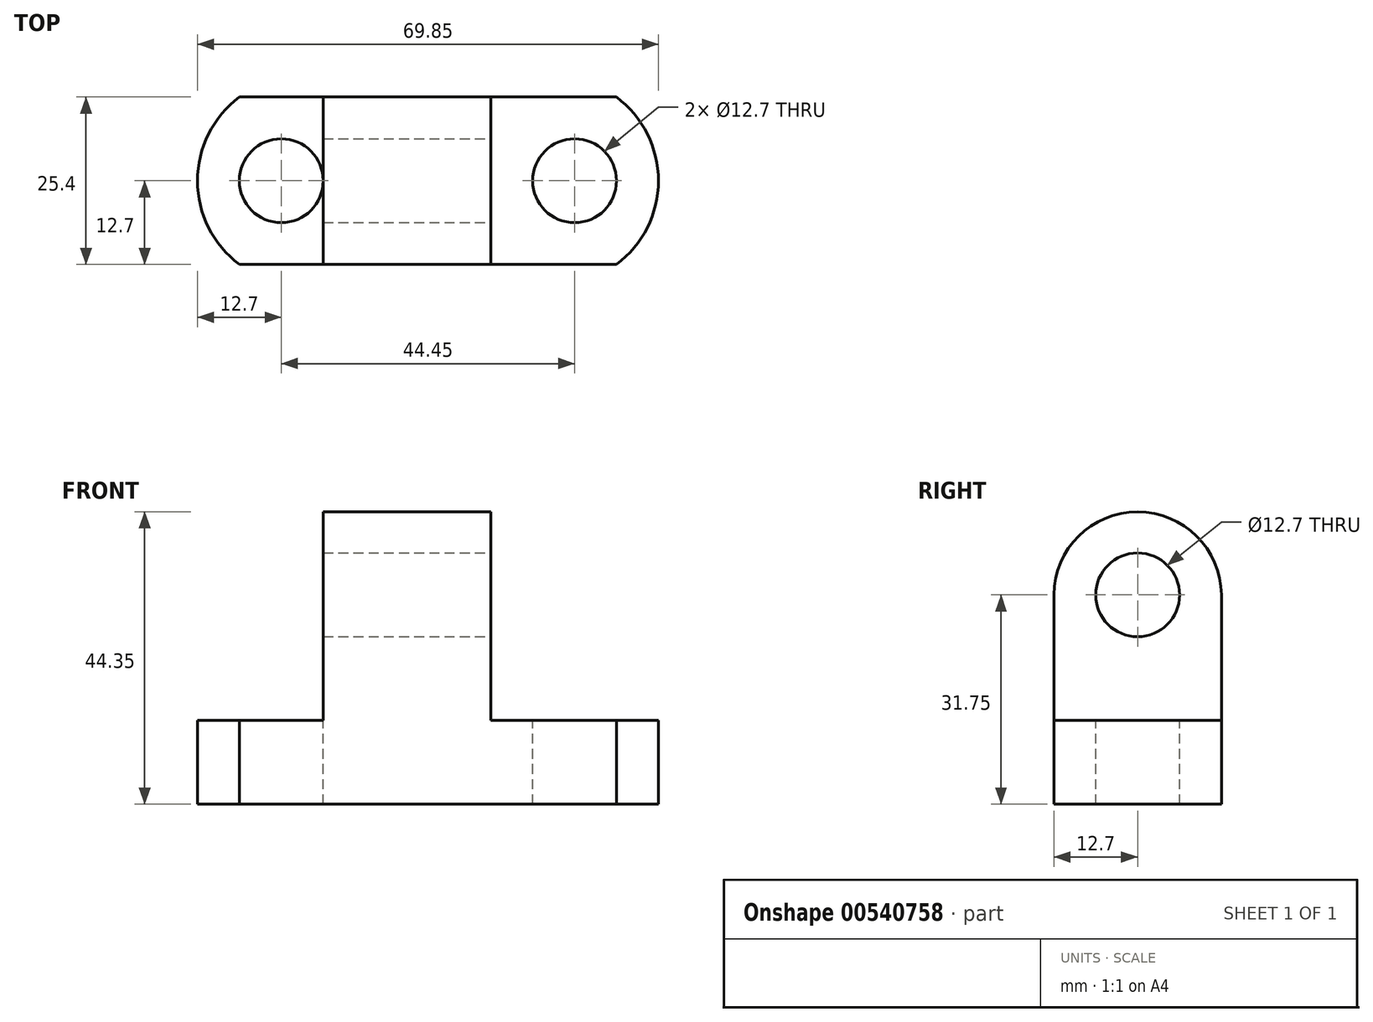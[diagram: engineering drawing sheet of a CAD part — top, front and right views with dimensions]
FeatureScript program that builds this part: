
annotation { "Feature Type Name" : "Feature", "Feature Type Description" : "" }
export const myFeature = defineFeature(function(context is Context, id is Id, definition is map)
    precondition{}
    {
        {
            var Q0;
            Q0=qCreatedBy(makeId("Front.planeOp"),FACE);
            var sketch = newSketch(context, id + "F0", { "sketchPlane" : qUnion([Q0])});
            skLineSegment(sketch, "E0", {"start": v(0, 0) * mm, "end": v(69.85, 0) * mm});
            skLineSegment(sketch, "E1", {"start": v(69.85, 0) * mm, "end": v(69.85, 12.7) * mm});
            skLineSegment(sketch, "E2", {"start": v(69.85, 12.7) * mm, "end": v(44.45, 12.7) * mm});
            skLineSegment(sketch, "E3", {"start": v(44.45, 12.7) * mm, "end": v(44.45, 44.45) * mm});
            skLineSegment(sketch, "E4", {"start": v(44.45, 44.45) * mm, "end": v(19.05, 44.45) * mm});
            skLineSegment(sketch, "E5", {"start": v(19.05, 44.45) * mm, "end": v(19.05, 12.7) * mm});
            skLineSegment(sketch, "E6", {"start": v(19.05, 12.7) * mm, "end": v(0, 12.7) * mm});
            skLineSegment(sketch, "E7", {"start": v(0, 12.7) * mm, "end": v(0, 0) * mm});
            skSolve(sketch);
        }
        {
            var Q0;
            Q0 = qSketchRegion(id + "F0", true);
            extrude(context, id + "F1", {"entities" : qUnion([Q0]), "depth" : 25.4 * mm, "offsetDistance" : 25.4 * mm});
        }
        {
            var Q0;
            Q0=makeQuery(id+"F1.opExtrude","SWEPT_FACE",FACE,{"disambiguationData":[OSD([sQuery(id+"F0.wireOp",EDGE,"E2")])]});
            var sketch = newSketch(context, id + "F2", { "sketchPlane" : qUnion([Q0])});
            skCircle(sketch, "E8", {"center": v(57.15, -12.7) * mm, "radius": 6.35 * mm});
            skPoint(sketch, "E8.centerSnap0", {"position": v(57.15, 0) * mm});
            skArc(sketch, "E9", {"start": v(63.5, -25.4) * mm, "mid": v(69.85, -12.7) * mm, "end": v(63.5, 0) * mm});
            skCircle(sketch, "E10", {"center": v(12.7, -12.7) * mm, "radius": 6.35 * mm});
            skSolve(sketch);
        }
        {
            var Q0;
            Q0=makeQuery(id+"F2.imprint","IMPRINT",FACE,{"disambiguationData":[TD([[makeQuery(id+"F2.imprint","IMPRINT",EDGE,{"derivedFrom":sQuery(id+"F2.wireOp",EDGE,"E10")}),1.0]])]});
            var Q1;
            Q1=makeQuery(id+"F2.imprint","IMPRINT",FACE,{"disambiguationData":[TD([[makeQuery(id+"F2.imprint","IMPRINT",EDGE,{"derivedFrom":sQuery(id+"F2.wireOp",EDGE,"E8")}),1.0]])]});
            var Q2;
            {var subQ0=sQuery(id+"F2.wireOp",EDGE,"E9");var subQ1=sQuery(id+"F0.wireOp",EDGE,"E2");var subQ2=makeQuery(id+"F1.opExtrude","CAP_EDGE",EDGE,{"disambiguationData":[OSD([subQ1])],"isStart":false});var subQ3=makeQuery(id+"F2.imprint","INTERSECT",VERTEX,{"derivedFrom":[subQ2,subQ0]});Q2=makeQuery(id+"F2.imprint","IMPRINT",FACE,{"disambiguationData":[TD([[makeQuery(id+"F2.imprint","IMPRINT",EDGE,{"disambiguationData":[TD([[subQ3,-1.0]])],"derivedFrom":subQ0}),-1.0]])]});}
            var Q3;
            {var subQ0=sQuery(id+"F2.wireOp",EDGE,"E9");var subQ1=sQuery(id+"F0.wireOp",EDGE,"E2");var subQ2=makeQuery(id+"F1.opExtrude","CAP_EDGE",EDGE,{"disambiguationData":[OSD([subQ1])],"isStart":true});var subQ3=makeQuery(id+"F2.imprint","INTERSECT",VERTEX,{"derivedFrom":[subQ2,subQ0]});Q3=makeQuery(id+"F2.imprint","IMPRINT",FACE,{"disambiguationData":[TD([[makeQuery(id+"F2.imprint","IMPRINT",EDGE,{"disambiguationData":[TD([[subQ3,1.0]])],"derivedFrom":subQ0}),-1.0]])]});}
            extrude(context, id + "F3", {"entities" : qUnion([Q0, Q1, Q2, Q3]), "operationType" : NewBodyOperationType.REMOVE, "oppositeDirection" : true, "depth" : 25.4 * mm, "offsetDistance" : 25.4 * mm});
        }
        {
            var Q0;
            Q0=makeQuery(id+"F1.opExtrude","SWEPT_FACE",FACE,{"disambiguationData":[OSD([sQuery(id+"F0.wireOp",EDGE,"E6")])]});
            var sketch = newSketch(context, id + "F4", { "sketchPlane" : qUnion([Q0])});
            skArc(sketch, "E11", {"start": v(6.35, 0) * mm, "mid": v(0, -12.7) * mm, "end": v(6.35, -25.4) * mm});
            skSolve(sketch);
        }
        {
            var Q0;
            {var subQ0=sQuery(id+"F4.wireOp",EDGE,"E11");var subQ1=sQuery(id+"F0.wireOp",EDGE,"E6");var subQ2=makeQuery(id+"F1.opExtrude","CAP_EDGE",EDGE,{"disambiguationData":[OSD([subQ1])],"isStart":true});var subQ3=makeQuery(id+"F4.imprint","INTERSECT",VERTEX,{"derivedFrom":[subQ2,subQ0]});Q0=makeQuery(id+"F4.imprint","IMPRINT",FACE,{"disambiguationData":[TD([[makeQuery(id+"F4.imprint","IMPRINT",EDGE,{"disambiguationData":[TD([[subQ3,-1.0]])],"derivedFrom":subQ0}),-1.0]])]});}
            var Q1;
            {var subQ0=sQuery(id+"F4.wireOp",EDGE,"E11");var subQ1=sQuery(id+"F0.wireOp",EDGE,"E6");var subQ2=makeQuery(id+"F1.opExtrude","CAP_EDGE",EDGE,{"disambiguationData":[OSD([subQ1])],"isStart":false});var subQ3=makeQuery(id+"F4.imprint","INTERSECT",VERTEX,{"derivedFrom":[subQ2,subQ0]});Q1=makeQuery(id+"F4.imprint","IMPRINT",FACE,{"disambiguationData":[TD([[makeQuery(id+"F4.imprint","IMPRINT",EDGE,{"disambiguationData":[TD([[subQ3,1.0]])],"derivedFrom":subQ0}),-1.0]])]});}
            extrude(context, id + "F5", {"entities" : qUnion([Q0, Q1]), "operationType" : NewBodyOperationType.REMOVE, "oppositeDirection" : true, "depth" : 25.4 * mm, "offsetDistance" : 25.4 * mm});
        }
        {
            var Q0;
            Q0=makeQuery(id+"F1.opExtrude","SWEPT_FACE",FACE,{"disambiguationData":[OSD([sQuery(id+"F0.wireOp",EDGE,"E3")])]});
            var sketch = newSketch(context, id + "F6", { "sketchPlane" : qUnion([Q0])});
            skCircle(sketch, "E12", {"center": v(-12.7, 31.75) * mm, "radius": 6.35 * mm});
            skArc(sketch, "E13", {"start": v(0, 31.75) * mm, "mid": v(-12.7, 44.35) * mm, "end": v(-25.4, 31.75) * mm});
            skSolve(sketch);
        }
        {
            var Q0;
            {var subQ0=sQuery(id+"F6.wireOp",EDGE,"E13");Q0=makeQuery(id+"F6.imprint","IMPRINT",FACE,{"disambiguationData":[TD([[makeQuery(id+"F6.imprint","IMPRINT",EDGE,{"derivedFrom":subQ0}),-1.0]])]});}
            var Q1;
            Q1=makeQuery(id+"F6.imprint","IMPRINT",FACE,{"disambiguationData":[TD([[makeQuery(id+"F6.imprint","IMPRINT",EDGE,{"derivedFrom":sQuery(id+"F6.wireOp",EDGE,"E12")}),1.0]])]});
            extrude(context, id + "F7", {"entities" : qUnion([Q0, Q1]), "operationType" : NewBodyOperationType.REMOVE, "oppositeDirection" : true, "depth" : 25.4 * mm, "offsetDistance" : 25.4 * mm});
        }
    });
